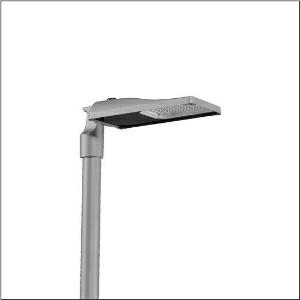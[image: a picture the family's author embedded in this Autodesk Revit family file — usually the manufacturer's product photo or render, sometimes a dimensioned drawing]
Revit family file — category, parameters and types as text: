
# Revit family: streetlight_sl_31_mini___st1_0a_5xh2d31s08ha_0250
name_source: partatom
category: Lighting Fixtures
units: mm (PartAtom-declared; Revit-internal decimal feet)

## family parameters
Cut with Voids When Loaded = No
Host = Face
Light Source = No
Part Type = Normal
Room Calculation Point = No
Round Connector Dimension = Use Diameter
Shared = No

## types (1)
- --- (1 x LED, 9230 lm, 68.3 W, 3000K)
    Apparent Load = 68 VA
    CIE Flux Codes = 37 72 97 100 100
    Color Rendering = 70
    Color Temperature = 3000K
    Default Elevation = 1800 mm
    Description = Streetlight SL 31 mini D4i, Desk-Remote mast luminaire for post-top, side-entry; light control with lens of PMMA; light distribution: ST1.0a, direct asymmetric distribution, for standard-compliant lighting for roads and squares; LED: luminous flux: 9.230lm, light colour: 730, colour temperature: 3000K; luminous efficacy: 135,1lm/W; control: pre-setting: logarithmic dimming characteristic, flexible luminous flux parameterisation, time-dependent luminous flux control, constant luminous flux control, power reduction, intelligent temperature release in ECG and LED module, overheat protection; luminaire housing, of diecast aluminium, SITECO metallic grey (DB 702S), corrosivity category C5 high according to DIN EN ISO 12944; cover of toughened safety glass, transparent, mast flange of diecast aluminium, SITECO metallic grey (DB 702S), spigot size: 76/60mm, mast flange included unmounted; with cable H07RN-F 2x 1.5mm², cable length: 8,5m, connection cable pre-assembled; mains connection: 220..240V, AC, 50/60Hz; power consumption (at start of service life): 68,3W / (at end of service life): 74,5W / (with reduced operation 50%): 29,5W; protection rating (complete): IP66; insulation class (complete): insulation class II (safety insulation); impact resistance: IK10; certification: CE, ENEC, ENEC+, VDE, UKCA, ZD4i; permissible operating ambient temperature for outdoor applications: -40..+50°C; packaging unit: 1 piece

Light Distribution: ST1.0a
    Height = 76 mm
    Lamp = 1 x LED
    Lamp Light Flux = 9230 lm
    Lamp Power = 68.3 W
    Lamp count = 1
    Length = 547 mm
    Luminous efficacy = 135 lm/W
    Manufacturer = Siteco
    ModVariant = No
    Model = 5XH2D31S08HA
    Number of Poles = 1
    OnlyDefault = Yes
    Power Factor = 1
    Product Name = Streetlight SL 31 mini | ST1.0a
    Product group = mast luminaire | pylon top
    ProductGroupID = 6100
    Protection Class = Protection class II
    Protection Degree = IP 66
    RLX_Detail_Level = 1
    RLX_Emergency_Light_Flux = 0 lm
    RLX_Emergency_Type = 0
    RLX_Emergency_Type_DB = No
    RlxData = <blob elided: 39517 chars, md5=ee7d1930>
    Socket = socket
    Standby Power = 0 W
    System Light Flux = 9230 lm
    System Power = 68 W
    Type Comments = factory setting: luminous flux: 100 % | dim-lin: 254 | 692 mA
    Type Image = l_1300330.jpg
    URL = http://relux.com
    VarID = @adj_020663
    Voltage = 0 V
    Weight = 0.00 kg
    Width = 265 mm

## geometry (parser evidence)
native form markers: Blend x4, Sweep x10
no freeform markers — native parametric forms only
